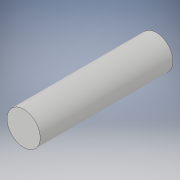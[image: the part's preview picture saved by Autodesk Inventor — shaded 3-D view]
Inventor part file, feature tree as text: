
AUTODESK INVENTOR PART (.ipt)
format: ipt  version: 2019 (Build 230136000, 136)  size: 90,112 bytes
history: native  units: mm
features: other x1, extrude x1, sketch x1
ambient origin geometry x8: Origin, YZ Plane, XZ Plane, XY Plane, X Axis, Y Axis, Z Axis, Center Point
bodies: Body1 (feature_tree)
feature tree (3):
  other  "實體1"
  extrude  "擠出1"  Depth=10.0mm
  sketch  "草圖1"
